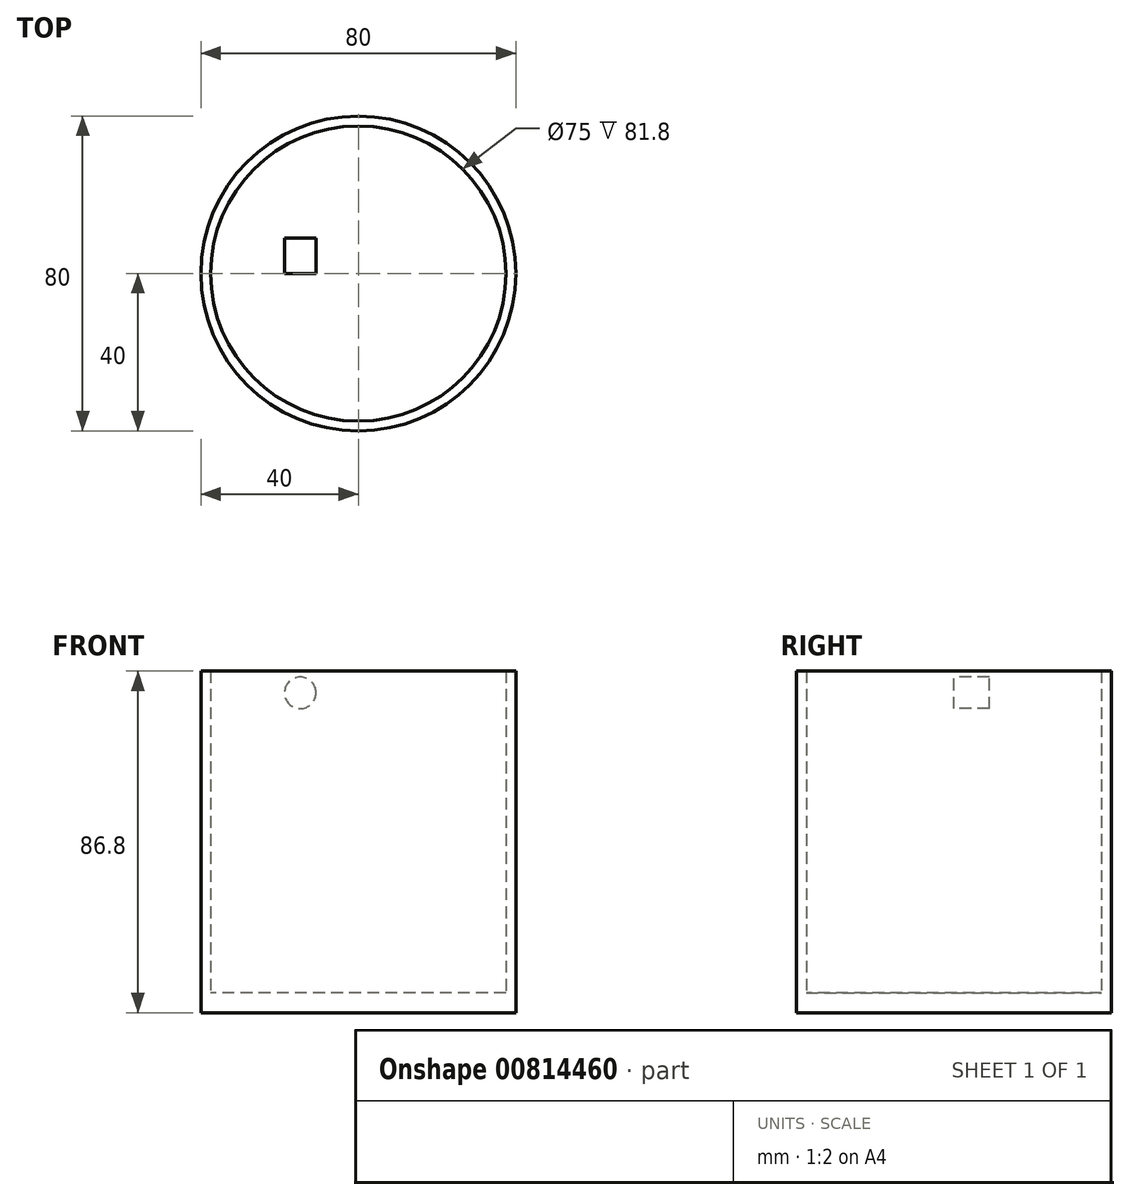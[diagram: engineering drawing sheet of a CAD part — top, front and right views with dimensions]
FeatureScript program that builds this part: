
annotation { "Feature Type Name" : "Feature", "Feature Type Description" : "" }
export const myFeature = defineFeature(function(context is Context, id is Id, definition is map)
    precondition{}
    {
        {
            var Q0;
            Q0=qCreatedBy(makeId("Top.planeOp"),FACE);
            var sketch = newSketch(context, id + "F0", { "sketchPlane" : qUnion([Q0])});
            skCircle(sketch, "E0", {"center": v(0, 0) * mm, "radius": 40 * mm});
            skCircle(sketch, "E1", {"center": v(0, 0) * mm, "radius": 37.5 * mm});
            skSolve(sketch);
        }
        {
            var Q0;
            Q0=makeQuery(id+"F0.imprint","IMPRINT",FACE,{"disambiguationData":[TD([[makeQuery(id+"F0.imprint","IMPRINT",EDGE,{"derivedFrom":sQuery(id+"F0.wireOp",EDGE,"E0")}),1.0]])]});
            var sketch = newSketch(context, id + "F1", { "sketchPlane" : qUnion([Q0])});
            skSolve(sketch);
        }
        {
            var Q0;
            Q0 = qSketchRegion(id + "F1", true);
            var Q1;
            Q1=makeQuery(id+"F0.imprint","IMPRINT",FACE,{"disambiguationData":[TD([[makeQuery(id+"F0.imprint","IMPRINT",EDGE,{"derivedFrom":sQuery(id+"F0.wireOp",EDGE,"E0")}),1.0]])]});
            extrude(context, id + "F2", {"entities" : qUnion([Q0, Q1]), "depth" : 86.8 * mm, "offsetDistance" : 25 * mm});
        }
        {
            var Q0;
            Q0=makeQuery(id+"F1.imprint","IMPRINT",FACE,{"disambiguationData":[TD([[makeQuery(id+"F1.imprint","IMPRINT",EDGE,{"derivedFrom":makeQuery(id+"F0.imprint","IMPRINT",EDGE,{"derivedFrom":sQuery(id+"F0.wireOp",EDGE,"E1")})}),1.0]])]});
            extrude(context, id + "F3", {"entities" : qUnion([Q0]), "operationType" : NewBodyOperationType.ADD, "depth" : 5 * mm, "offsetDistance" : 25 * mm});
        }
        {
            var Q0;
            Q0=qCreatedBy(makeId("Front.planeOp"),FACE);
            var sketch = newSketch(context, id + "F4", { "sketchPlane" : qUnion([Q0])});
            skCircle(sketch, "E2", {"center": v(-20.21, 52.1) * mm, "radius": 4 * mm});
            skCircle(sketch, "E3", {"center": v(-20.21, 25.35) * mm, "radius": 4 * mm});
            skCircle(sketch, "E4", {"center": v(-5.93, 38.12) * mm, "radius": 4 * mm});
            skCircle(sketch, "E5", {"center": v(6.84, 56.05) * mm, "radius": 4 * mm});
            skCircle(sketch, "E6", {"center": v(18.08, 22) * mm, "radius": 4 * mm});
            skCircle(sketch, "E7", {"center": v(0, 13.2) * mm, "radius": 4 * mm});
            skCircle(sketch, "E8", {"center": v(19.6, 38.72) * mm, "radius": 4 * mm});
            skCircle(sketch, "E9", {"center": v(25.38, 62.12) * mm, "radius": 4 * mm});
            skCircle(sketch, "E10", {"center": v(0, 73.37) * mm, "radius": 4 * mm});
            skCircle(sketch, "E11", {"center": v(-16.87, 69.72) * mm, "radius": 4 * mm});
            skCircle(sketch, "E12", {"center": v(16.26, 70.94) * mm, "radius": 4 * mm});
            skCircle(sketch, "E13", {"center": v(25.38, 48.75) * mm, "radius": 4 * mm});
            skCircle(sketch, "E14", {"center": v(13.83, 8.33) * mm, "radius": 4 * mm});
            skCircle(sketch, "E15", {"center": v(-20.21, 5.9) * mm, "radius": 4 * mm});
            skCircle(sketch, "E16", {"center": v(-30.24, 15.32) * mm, "radius": 4 * mm});
            skCircle(sketch, "E17", {"center": v(-31.15, 61.21) * mm, "radius": 4 * mm});
            skCircle(sketch, "E18", {"center": v(-27.5, 39.94) * mm, "radius": 4 * mm});
            skCircle(sketch, "E19", {"center": v(-7.75, 54.83) * mm, "radius": 4 * mm});
            skCircle(sketch, "E20", {"center": v(31.15, 73.37) * mm, "radius": 4 * mm});
            skCircle(sketch, "E21", {"center": v(0, 26.57) * mm, "radius": 4 * mm});
            skCircle(sketch, "E22", {"center": v(31.46, 29.9) * mm, "radius": 4 * mm});
            skCircle(sketch, "E23", {"center": v(28.42, 12.59) * mm, "radius": 4 * mm});
            skCircle(sketch, "E24", {"center": v(-31.76, 77.02) * mm, "radius": 4 * mm});
            skCircle(sketch, "E25", {"center": v(-14.74, 81.27) * mm, "radius": 4 * mm});
            skCircle(sketch, "E26", {"center": v(7.14, 80.97) * mm, "radius": 4 * mm});
            skCircle(sketch, "E27", {"center": v(22.64, 81.27) * mm, "radius": 4 * mm});
            skSolve(sketch);
        }
        {
            var Q0;
            Q0=makeQuery(id+"F4.imprint","IMPRINT",FACE,{"disambiguationData":[TD([[makeQuery(id+"F4.imprint","IMPRINT",EDGE,{"derivedFrom":sQuery(id+"F4.wireOp",EDGE,"E25")}),1.0]])]});
            extrude(context, id + "F5", {"entities" : qUnion([Q0]), "oppositeDirection" : true, "depth" : 1 * mm, "offsetDistance" : 25 * mm});
        }
        {
            var Q0;
            Q0=makeQuery(id+"F5.opExtrude","CAP_FACE",FACE,{"disambiguationData":[OSD([sQuery(id+"F4.wireOp",EDGE,"E25")])],"isStart":true});
            extrude(context, id + "F6", {"entities" : qUnion([Q0]), "operationType" : NewBodyOperationType.ADD, "oppositeDirection" : true, "depth" : 9 * mm, "offsetDistance" : 25 * mm});
        }
    });
